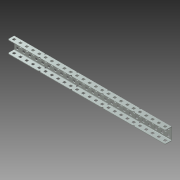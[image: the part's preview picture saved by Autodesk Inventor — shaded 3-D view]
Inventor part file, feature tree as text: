
AUTODESK INVENTOR PART (.ipt)
format: ipt  version: 2015 (Build 190159000, 159)  size: 2,724,864 bytes
history: native  units: mm (DEFAULTED — no unit token found)
features: other x124, extrude x124, pattern_linear x3, sketch x2, imported_body x1, plane x1, mirror x1
ambient origin geometry x8: Origin, YZ Plane, XZ Plane, XY Plane, X Axis, Y Axis, Z Axis, Center Point
bodies: Solid1 (feature_tree)
feature tree (256):
  imported_body  "Base1"
  sketch  "Sketch1"  dims[d1=1.1684mm]
  pattern_linear  "Rectangular Pattern1"  Spacing1=1.1684mm  [1 undecoded]
  pattern_linear  "Rectangular Pattern2"  Spacing1=0.0mm  [1 undecoded]
  pattern_linear  "Rectangular Pattern3"  Count1=25  [1 undecoded]
  plane  "Work Plane1"
  mirror  "Mirror1"
  other  "Srf1"
  other  "Srf2"
  other  "Srf3"
  other  "Srf4"
  other  "Srf5"
  other  "Srf6"
  other  "Srf7"
  other  "Srf8"
  other  "Srf9"
  other  "Srf10"
  other  "Srf11"
  other  "Srf12"
  other  "Srf13"
  other  "Srf14"
  other  "Srf15"
  other  "Srf16"
  other  "Srf17"
  other  "Srf18"
  other  "Srf19"
  other  "Srf20"
  other  "Srf21"
  other  "Srf22"
  other  "Srf23"
  other  "Srf24"
  other  "Srf25"
  other  "Srf26"
  other  "Srf27"
  other  "Srf28"
  other  "Srf29"
  other  "Srf30"
  other  "Srf31"
  other  "Srf32"
  other  "Srf33"
  other  "Srf34"
  other  "Srf35"
  other  "Srf36"
  other  "Srf37"
  other  "Srf38"
  other  "Srf39"
  other  "Srf40"
  other  "Srf41"
  other  "Srf42"
  other  "Srf43"
  other  "Srf44"
  other  "Srf45"
  other  "Srf46"
  other  "Srf47"
  other  "Srf48"
  other  "Srf49"
  other  "Srf50"
  other  "Srf51"
  other  "Srf52"
  other  "Srf53"
  other  "Srf54"
  other  "Srf55"
  other  "Srf56"
  other  "Srf57"
  other  "Srf58"
  other  "Srf59"
  other  "Srf60"
  other  "Srf61"
  other  "Srf62"
  other  "Srf63"
  other  "Srf64"
  other  "Srf65"
  other  "Srf66"
  other  "Srf67"
  other  "Srf68"
  other  "Srf69"
  other  "Srf70"
  other  "Srf71"
  other  "Srf72"
  other  "Srf73"
  other  "Srf74"
  sketch  "Sketch2"  dims[d2=0.0mm d3=1.1684mm d4=0.0mm d5=250.0mm d7=12.7mm d8=20.0mm d10=12.7mm d11=240.0mm d13=12.7mm d14=1.1684mm d15=0.0mm d16=250.0mm d18=12.7mm d19=0.0mm d20=0.0mm d21=0.0mm d22=0.0mm d23=0.0mm d24=0.0mm d25=0.0mm d26=0.0mm d27=0.0mm d28=0.0mm d29=0.0mm d30=0.0mm d31=0.0mm d32=0.0mm d33=0.0mm d34=0.0mm d35=0.0mm d36=0.0mm d37=0.0mm d38=0.0mm d39=0.0mm d40=0.0mm d41=0.0mm d42=0.0mm d43=0.0mm d44=0.0mm d45=0.0mm d46=0.0mm d47=0.0mm d48=0.0mm d49=0.0mm d50=0.0mm d51=0.0mm d52=0.0mm d53=0.0mm d54=0.0mm d55=0.0mm d56=0.0mm d57=0.0mm d58=0.0mm d59=0.0mm d60=0.0mm d61=0.0mm d62=0.0mm d63=0.0mm d64=0.0mm d65=0.0mm d66=0.0mm d67=0.0mm d68=0.0mm d69=0.0mm d70=0.0mm d71=0.0mm d72=0.0mm d73=0.0mm d74=0.0mm d75=0.0mm d76=0.0mm d77=0.0mm d78=0.0mm d79=0.0mm d80=0.0mm d81=0.0mm d82=0.0mm d83=0.0mm d84=0.0mm d85=0.0mm d86=0.0mm d87=0.0mm d88=0.0mm d89=0.0mm d90=0.0mm d91=0.0mm d92=0.0mm d93=0.0mm d94=0.0mm d95=0.0mm d96=0.0mm d97=0.0mm d98=0.0mm d99=0.0mm d100=0.0mm d101=0.0mm d102=0.0mm d103=0.0mm d104=0.0mm d105=0.0mm d106=0.0mm d107=0.0mm d108=0.0mm d109=0.0mm d110=0.0mm d111=0.0mm d112=0.0mm d113=0.0mm d114=0.0mm d115=0.0mm d116=0.0mm d117=0.0mm d118=0.0mm d119=0.0mm d120=0.0mm d121=0.0mm d122=0.0mm d123=0.0mm d124=0.0mm d125=0.0mm d126=0.0mm d127=0.0mm d128=0.0mm d129=0.0mm d130=0.0mm d131=0.0mm d132=0.0mm d133=0.0mm d134=0.0mm d135=0.0mm d136=0.0mm d137=0.0mm d138=0.0mm d139=0.0mm d140=0.0mm d141=0.0mm d142=0.0mm d143=0.0mm d144=0.0mm d145=0.0mm d146=0.0mm d147=0.0mm d148=0.0mm d149=0.0mm d150=0.0mm d151=0.0mm d152=0.0mm d153=0.0mm d154=0.0mm d155=0.0mm d156=0.0mm d157=0.0mm d158=0.0mm d159=0.0mm d160=0.0mm d161=0.0mm d162=0.0mm d163=0.0mm d164=0.0mm d165=0.0mm d166=0.0mm d167=0.0mm d168=0.0mm d169=0.0mm d170=0.0mm d171=0.0mm d172=0.0mm d173=0.0mm d174=0.0mm d175=0.0mm d176=0.0mm d177=0.0mm d178=0.0mm d179=0.0mm d180=0.0mm d181=0.0mm d182=0.0mm d183=0.0mm d184=0.0mm d185=0.0mm d186=0.0mm d187=0.0mm d188=0.0mm d189=0.0mm d190=0.0mm d191=0.0mm d192=0.0mm d193=0.0mm d194=0.0mm d195=0.0mm d196=0.0mm d197=0.0mm d198=0.0mm d199=0.0mm d200=0.0mm d201=0.0mm d202=0.0mm d203=0.0mm d204=0.0mm d205=0.0mm d206=0.0mm d207=0.0mm d208=0.0mm d209=0.0mm d210=0.0mm d211=0.0mm d212=0.0mm d213=0.0mm d214=0.0mm d215=0.0mm d216=0.0mm d217=0.0mm d218=0.0mm d219=0.0mm d220=0.0mm d221=0.0mm d222=0.0mm d223=0.0mm d224=0.0mm d225=0.0mm d226=0.0mm d227=0.0mm d228=0.0mm d229=0.0mm d230=0.0mm d231=0.0mm d232=0.0mm d233=0.0mm d234=0.0mm d235=0.0mm d236=0.0mm d237=0.0mm d238=0.0mm d239=0.0mm d240=0.0mm d241=0.0mm d242=0.0mm d243=0.0mm d244=0.0mm d245=0.0mm d246=0.0mm d247=0.0mm d248=0.0mm d249=0.0mm d250=0.0mm d251=0.0mm d252=0.0mm d253=0.0mm d254=0.0mm d255=0.0mm d256=0.0mm d257=0.0mm d258=0.0mm d259=0.0mm d260=0.0mm d261=0.0mm d262=0.0mm d263=0.0mm]
  other  "Srf75"
  other  "Srf76"
  other  "Srf77"
  other  "Srf78"
  other  "Srf79"
  other  "Srf80"
  other  "Srf81"
  other  "Srf82"
  other  "Srf83"
  other  "Srf84"
  other  "Srf85"
  other  "Srf86"
  other  "Srf87"
  other  "Srf88"
  other  "Srf89"
  other  "Srf90"
  other  "Srf91"
  other  "Srf92"
  other  "Srf93"
  other  "Srf94"
  other  "Srf95"
  other  "Srf96"
  other  "Srf97"
  other  "Srf98"
  other  "Srf99"
  other  "Srf100"
  other  "Srf101"
  other  "Srf102"
  other  "Srf103"
  other  "Srf104"
  other  "Srf105"
  other  "Srf106"
  other  "Srf107"
  other  "Srf108"
  other  "Srf109"
  other  "Srf110"
  other  "Srf111"
  other  "Srf112"
  other  "Srf113"
  other  "Srf114"
  other  "Srf115"
  other  "Srf116"
  other  "Srf117"
  other  "Srf118"
  other  "Srf119"
  other  "Srf120"
  other  "Srf121"
  other  "Srf122"
  other  "Srf123"
  other  "Srf124"
  extrude  "ExtrusionSrf1"  Depth=12.7mm
  extrude  "ExtrusionSrf2"  Depth=20.0mm
  extrude  "ExtrusionSrf75"  Depth=240.0mm
  extrude  "ExtrusionSrf3"  Depth=12.7mm
  extrude  "ExtrusionSrf4"  Depth=1.1684mm
  extrude  "ExtrusionSrf5"  TaperAngle=0.0deg  [1 undecoded]
  extrude  "ExtrusionSrf6"  Depth=250.0mm
  extrude  "ExtrusionSrf7"  Depth=12.7mm
  extrude  "ExtrusionSrf8"  TaperAngle=0.0deg  [1 undecoded]
  extrude  "ExtrusionSrf9"  TaperAngle=0.0deg  [1 undecoded]
  extrude  "ExtrusionSrf10"  TaperAngle=0.0deg  [1 undecoded]
  extrude  "ExtrusionSrf11"  TaperAngle=0.0deg  [1 undecoded]
  extrude  "ExtrusionSrf12"  TaperAngle=0.0deg  [1 undecoded]
  extrude  "ExtrusionSrf13"  TaperAngle=0.0deg  [1 undecoded]
  extrude  "ExtrusionSrf14"  TaperAngle=0.0deg  [1 undecoded]
  extrude  "ExtrusionSrf15"  TaperAngle=0.0deg  [1 undecoded]
  extrude  "ExtrusionSrf16"  TaperAngle=0.0deg  [1 undecoded]
  extrude  "ExtrusionSrf17"  TaperAngle=0.0deg  [1 undecoded]
  extrude  "ExtrusionSrf18"  TaperAngle=0.0deg  [1 undecoded]
  extrude  "ExtrusionSrf19"  TaperAngle=0.0deg  [1 undecoded]
  extrude  "ExtrusionSrf20"  TaperAngle=0.0deg  [1 undecoded]
  extrude  "ExtrusionSrf21"  TaperAngle=0.0deg  [1 undecoded]
  extrude  "ExtrusionSrf22"  TaperAngle=0.0deg  [1 undecoded]
  extrude  "ExtrusionSrf23"  TaperAngle=0.0deg  [1 undecoded]
  extrude  "ExtrusionSrf24"  TaperAngle=0.0deg  [1 undecoded]
  extrude  "ExtrusionSrf25"  TaperAngle=0.0deg  [1 undecoded]
  extrude  "ExtrusionSrf26"  TaperAngle=0.0deg  [1 undecoded]
  extrude  "ExtrusionSrf27"  TaperAngle=0.0deg  [1 undecoded]
  extrude  "ExtrusionSrf28"  TaperAngle=0.0deg  [1 undecoded]
  extrude  "ExtrusionSrf29"  TaperAngle=0.0deg  [1 undecoded]
  extrude  "ExtrusionSrf30"  TaperAngle=0.0deg  [1 undecoded]
  extrude  "ExtrusionSrf31"  TaperAngle=0.0deg  [1 undecoded]
  extrude  "ExtrusionSrf32"  TaperAngle=0.0deg  [1 undecoded]
  extrude  "ExtrusionSrf33"  TaperAngle=0.0deg  [1 undecoded]
  extrude  "ExtrusionSrf34"  TaperAngle=0.0deg  [1 undecoded]
  extrude  "ExtrusionSrf35"  TaperAngle=0.0deg  [1 undecoded]
  extrude  "ExtrusionSrf36"  TaperAngle=0.0deg  [1 undecoded]
  extrude  "ExtrusionSrf37"  TaperAngle=0.0deg  [1 undecoded]
  extrude  "ExtrusionSrf38"  TaperAngle=0.0deg  [1 undecoded]
  extrude  "ExtrusionSrf39"  TaperAngle=0.0deg  [1 undecoded]
  extrude  "ExtrusionSrf40"  TaperAngle=0.0deg  [1 undecoded]
  extrude  "ExtrusionSrf41"  TaperAngle=0.0deg  [1 undecoded]
  extrude  "ExtrusionSrf42"  TaperAngle=0.0deg  [1 undecoded]
  extrude  "ExtrusionSrf43"  TaperAngle=0.0deg  [1 undecoded]
  extrude  "ExtrusionSrf44"  TaperAngle=0.0deg  [1 undecoded]
  extrude  "ExtrusionSrf45"  TaperAngle=0.0deg  [1 undecoded]
  extrude  "ExtrusionSrf46"  TaperAngle=0.0deg  [1 undecoded]
  extrude  "ExtrusionSrf47"  TaperAngle=0.0deg  [1 undecoded]
  extrude  "ExtrusionSrf48"  TaperAngle=0.0deg  [1 undecoded]
  extrude  "ExtrusionSrf49"  TaperAngle=0.0deg  [1 undecoded]
  extrude  "ExtrusionSrf50"  TaperAngle=0.0deg  [1 undecoded]
  extrude  "ExtrusionSrf51"  TaperAngle=0.0deg  [1 undecoded]
  extrude  "ExtrusionSrf52"  TaperAngle=0.0deg  [1 undecoded]
  extrude  "ExtrusionSrf53"  TaperAngle=0.0deg  [1 undecoded]
  extrude  "ExtrusionSrf54"  TaperAngle=0.0deg  [1 undecoded]
  extrude  "ExtrusionSrf55"  TaperAngle=0.0deg  [1 undecoded]
  extrude  "ExtrusionSrf56"  TaperAngle=0.0deg  [1 undecoded]
  extrude  "ExtrusionSrf57"  TaperAngle=0.0deg  [1 undecoded]
  extrude  "ExtrusionSrf58"  TaperAngle=0.0deg  [1 undecoded]
  extrude  "ExtrusionSrf59"  TaperAngle=0.0deg  [1 undecoded]
  extrude  "ExtrusionSrf60"  TaperAngle=0.0deg  [1 undecoded]
  extrude  "ExtrusionSrf61"  TaperAngle=0.0deg  [1 undecoded]
  extrude  "ExtrusionSrf62"  TaperAngle=0.0deg  [1 undecoded]
  extrude  "ExtrusionSrf63"  TaperAngle=0.0deg  [1 undecoded]
  extrude  "ExtrusionSrf64"  TaperAngle=0.0deg  [1 undecoded]
  extrude  "ExtrusionSrf65"  TaperAngle=0.0deg  [1 undecoded]
  extrude  "ExtrusionSrf66"  TaperAngle=0.0deg  [1 undecoded]
  extrude  "ExtrusionSrf67"  TaperAngle=0.0deg  [1 undecoded]
  extrude  "ExtrusionSrf68"  TaperAngle=0.0deg  [1 undecoded]
  extrude  "ExtrusionSrf69"  TaperAngle=0.0deg  [1 undecoded]
  extrude  "ExtrusionSrf70"  TaperAngle=0.0deg  [1 undecoded]
  extrude  "ExtrusionSrf71"  TaperAngle=0.0deg  [1 undecoded]
  extrude  "ExtrusionSrf72"  TaperAngle=0.0deg  [1 undecoded]
  extrude  "ExtrusionSrf73"  TaperAngle=0.0deg  [1 undecoded]
  extrude  "ExtrusionSrf74"  TaperAngle=0.0deg  [1 undecoded]
  extrude  "ExtrusionSrf76"  TaperAngle=0.0deg  [1 undecoded]
  extrude  "ExtrusionSrf77"  TaperAngle=0.0deg  [1 undecoded]
  extrude  "ExtrusionSrf78"  TaperAngle=0.0deg  [1 undecoded]
  extrude  "ExtrusionSrf79"  TaperAngle=0.0deg  [1 undecoded]
  extrude  "ExtrusionSrf80"  TaperAngle=0.0deg  [1 undecoded]
  extrude  "ExtrusionSrf81"  TaperAngle=0.0deg  [1 undecoded]
  extrude  "ExtrusionSrf82"  TaperAngle=0.0deg  [1 undecoded]
  extrude  "ExtrusionSrf83"  TaperAngle=0.0deg  [1 undecoded]
  extrude  "ExtrusionSrf84"  TaperAngle=0.0deg  [1 undecoded]
  extrude  "ExtrusionSrf85"  TaperAngle=0.0deg  [1 undecoded]
  extrude  "ExtrusionSrf86"  TaperAngle=0.0deg  [1 undecoded]
  extrude  "ExtrusionSrf87"  TaperAngle=0.0deg  [1 undecoded]
  extrude  "ExtrusionSrf88"  TaperAngle=0.0deg  [1 undecoded]
  extrude  "ExtrusionSrf89"  TaperAngle=0.0deg  [1 undecoded]
  extrude  "ExtrusionSrf90"  TaperAngle=0.0deg  [1 undecoded]
  extrude  "ExtrusionSrf91"  TaperAngle=0.0deg  [1 undecoded]
  extrude  "ExtrusionSrf92"  TaperAngle=0.0deg  [1 undecoded]
  extrude  "ExtrusionSrf93"  TaperAngle=0.0deg  [1 undecoded]
  extrude  "ExtrusionSrf94"  TaperAngle=0.0deg  [1 undecoded]
  extrude  "ExtrusionSrf95"  TaperAngle=0.0deg  [1 undecoded]
  extrude  "ExtrusionSrf96"  TaperAngle=0.0deg  [1 undecoded]
  extrude  "ExtrusionSrf97"  TaperAngle=0.0deg  [1 undecoded]
  extrude  "ExtrusionSrf98"  TaperAngle=0.0deg  [1 undecoded]
  extrude  "ExtrusionSrf99"  TaperAngle=0.0deg  [1 undecoded]
  extrude  "ExtrusionSrf100"  TaperAngle=0.0deg  [1 undecoded]
  extrude  "ExtrusionSrf101"  TaperAngle=0.0deg  [1 undecoded]
  extrude  "ExtrusionSrf102"  TaperAngle=0.0deg  [1 undecoded]
  extrude  "ExtrusionSrf103"  TaperAngle=0.0deg  [1 undecoded]
  extrude  "ExtrusionSrf104"  TaperAngle=0.0deg  [1 undecoded]
  extrude  "ExtrusionSrf105"  TaperAngle=0.0deg  [1 undecoded]
  extrude  "ExtrusionSrf106"  TaperAngle=0.0deg  [1 undecoded]
  extrude  "ExtrusionSrf107"  TaperAngle=0.0deg  [1 undecoded]
  extrude  "ExtrusionSrf108"  TaperAngle=0.0deg  [1 undecoded]
  extrude  "ExtrusionSrf109"  TaperAngle=0.0deg  [1 undecoded]
  extrude  "ExtrusionSrf110"  TaperAngle=0.0deg  [1 undecoded]
  extrude  "ExtrusionSrf111"  TaperAngle=0.0deg  [1 undecoded]
  extrude  "ExtrusionSrf112"  TaperAngle=0.0deg  [1 undecoded]
  extrude  "ExtrusionSrf113"  TaperAngle=0.0deg  [1 undecoded]
  extrude  "ExtrusionSrf114"  TaperAngle=0.0deg  [1 undecoded]
  extrude  "ExtrusionSrf115"  TaperAngle=0.0deg  [1 undecoded]
  extrude  "ExtrusionSrf116"  TaperAngle=0.0deg  [1 undecoded]
  extrude  "ExtrusionSrf117"  TaperAngle=0.0deg  [1 undecoded]
  extrude  "ExtrusionSrf118"  TaperAngle=0.0deg  [1 undecoded]
  extrude  "ExtrusionSrf119"  TaperAngle=0.0deg  [1 undecoded]
  extrude  "ExtrusionSrf120"  TaperAngle=0.0deg  [1 undecoded]
  extrude  "ExtrusionSrf121"  TaperAngle=0.0deg  [1 undecoded]
  extrude  "ExtrusionSrf122"  TaperAngle=0.0deg  [1 undecoded]
  extrude  "ExtrusionSrf123"  TaperAngle=0.0deg  [1 undecoded]
  extrude  "ExtrusionSrf124"  TaperAngle=0.0deg  [1 undecoded]
note: 120 required parameter values undecoded (feature->parameter linkage not recoverable at this tier; creation-order binding heuristic only, values carry confidence <= 0.55)
